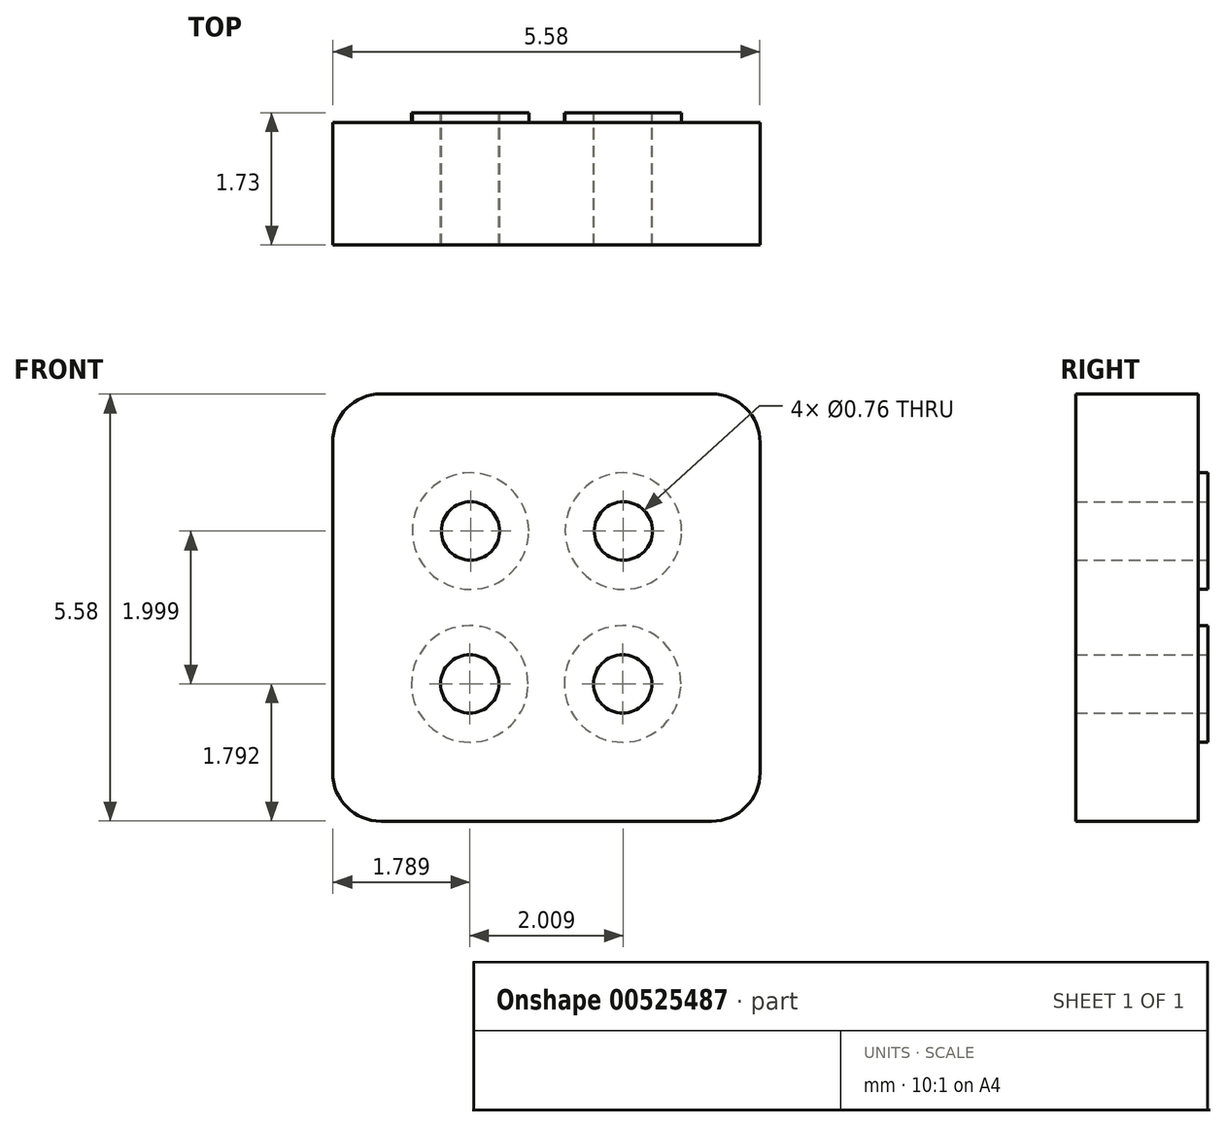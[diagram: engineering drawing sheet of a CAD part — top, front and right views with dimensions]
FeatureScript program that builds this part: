
annotation { "Feature Type Name" : "Feature", "Feature Type Description" : "" }
export const myFeature = defineFeature(function(context is Context, id is Id, definition is map)
    precondition{}
    {
        {
            var Q0;
            Q0=qCreatedBy(makeId("Front.planeOp"),FACE);
            var sketch = newSketch(context, id + "F0", { "sketchPlane" : qUnion([Q0])});
            skLineSegment(sketch, "E0.bottom", {"start": v(2.16, -2.8) * mm, "end": v(-2.16, -2.8) * mm});
            skLineSegment(sketch, "E0.top", {"start": v(2.16, 2.8) * mm, "end": v(-2.16, 2.8) * mm});
            skLineSegment(sketch, "E0.left", {"start": v(2.8, -2.16) * mm, "end": v(2.8, 2.16) * mm});
            skLineSegment(sketch, "E0.right", {"start": v(-2.8, -2.16) * mm, "end": v(-2.8, 2.16) * mm});
            skPoint(sketch, "E0.middle", {"position": v(0, 0) * mm});
            skCircle(sketch, "E1", {"center": v(-1, 1) * mm, "radius": 0.38 * mm});
            skCircle(sketch, "E2", {"center": v(1, 1) * mm, "radius": 0.38 * mm});
            skCircle(sketch, "E3", {"center": v(-1, -1) * mm, "radius": 0.38 * mm});
            skCircle(sketch, "E4", {"center": v(1, -1) * mm, "radius": 0.38 * mm});
            skCircle(sketch, "E5", {"center": v(-1, 1) * mm, "radius": 0.76 * mm});
            skCircle(sketch, "E6", {"center": v(1, 1) * mm, "radius": 0.76 * mm});
            skCircle(sketch, "E7", {"center": v(1, -1) * mm, "radius": 0.76 * mm});
            skCircle(sketch, "E8", {"center": v(-1, -1) * mm, "radius": 0.76 * mm});
            skPoint(sketch, "E9.visualSharp", {"position": v(2.8, 2.8) * mm});
            skArc(sketch, "E9.filletArc", {"start": v(2.8, 2.16) * mm, "mid": v(2.6, 2.6) * mm, "end": v(2.16, 2.8) * mm});
            skPoint(sketch, "E10.visualSharp", {"position": v(-2.8, 2.8) * mm});
            skArc(sketch, "E10.filletArc", {"start": v(-2.16, 2.8) * mm, "mid": v(-2.6, 2.6) * mm, "end": v(-2.8, 2.16) * mm});
            skPoint(sketch, "E11.visualSharp", {"position": v(-2.8, -2.8) * mm});
            skArc(sketch, "E11.filletArc", {"start": v(-2.8, -2.16) * mm, "mid": v(-2.6, -2.6) * mm, "end": v(-2.16, -2.8) * mm});
            skPoint(sketch, "E12.visualSharp", {"position": v(2.8, -2.8) * mm});
            skArc(sketch, "E12.filletArc", {"start": v(2.16, -2.8) * mm, "mid": v(2.6, -2.6) * mm, "end": v(2.8, -2.16) * mm});
            skSolve(sketch);
        }
        {
            var Q0;
            Q0=makeQuery(id+"F0.imprint","IMPRINT",FACE,{"disambiguationData":[TD([[makeQuery(id+"F0.imprint","IMPRINT",EDGE,{"derivedFrom":sQuery(id+"F0.wireOp",EDGE,"E0.bottom")}),-1.0]])]});
            var Q1;
            Q1=makeQuery(id+"F0.imprint","IMPRINT",FACE,{"disambiguationData":[TD([[makeQuery(id+"F0.imprint","IMPRINT",EDGE,{"derivedFrom":sQuery(id+"F0.wireOp",EDGE,"E1")}),-1.0]])]});
            var Q2;
            Q2=makeQuery(id+"F0.imprint","IMPRINT",FACE,{"disambiguationData":[TD([[makeQuery(id+"F0.imprint","IMPRINT",EDGE,{"derivedFrom":sQuery(id+"F0.wireOp",EDGE,"E2")}),-1.0]])]});
            var Q3;
            Q3=makeQuery(id+"F0.imprint","IMPRINT",FACE,{"disambiguationData":[TD([[makeQuery(id+"F0.imprint","IMPRINT",EDGE,{"derivedFrom":sQuery(id+"F0.wireOp",EDGE,"E4")}),-1.0]])]});
            var Q4;
            Q4=makeQuery(id+"F0.imprint","IMPRINT",FACE,{"disambiguationData":[TD([[makeQuery(id+"F0.imprint","IMPRINT",EDGE,{"derivedFrom":sQuery(id+"F0.wireOp",EDGE,"E3")}),-1.0]])]});
            extrude(context, id + "F1", {"entities" : qUnion([Q0, Q1, Q2, Q3, Q4]), "depth" : 1.6 * mm, "offsetDistance" : 25.4 * mm});
        }
        {
            var Q0;
            Q0=makeQuery(id+"F0.imprint","IMPRINT",FACE,{"disambiguationData":[TD([[makeQuery(id+"F0.imprint","IMPRINT",EDGE,{"derivedFrom":sQuery(id+"F0.wireOp",EDGE,"E2")}),-1.0]])]});
            var Q1;
            Q1=makeQuery(id+"F0.imprint","IMPRINT",FACE,{"disambiguationData":[TD([[makeQuery(id+"F0.imprint","IMPRINT",EDGE,{"derivedFrom":sQuery(id+"F0.wireOp",EDGE,"E4")}),-1.0]])]});
            var Q2;
            Q2=makeQuery(id+"F0.imprint","IMPRINT",FACE,{"disambiguationData":[TD([[makeQuery(id+"F0.imprint","IMPRINT",EDGE,{"derivedFrom":sQuery(id+"F0.wireOp",EDGE,"E3")}),-1.0]])]});
            var Q3;
            Q3=makeQuery(id+"F0.imprint","IMPRINT",FACE,{"disambiguationData":[TD([[makeQuery(id+"F0.imprint","IMPRINT",EDGE,{"derivedFrom":sQuery(id+"F0.wireOp",EDGE,"E1")}),-1.0]])]});
            extrude(context, id + "F2", {"entities" : qUnion([Q0, Q1, Q2, Q3]), "operationType" : NewBodyOperationType.ADD, "oppositeDirection" : true, "depth" : 0.13 * mm, "offsetDistance" : 25.4 * mm});
        }
    });
